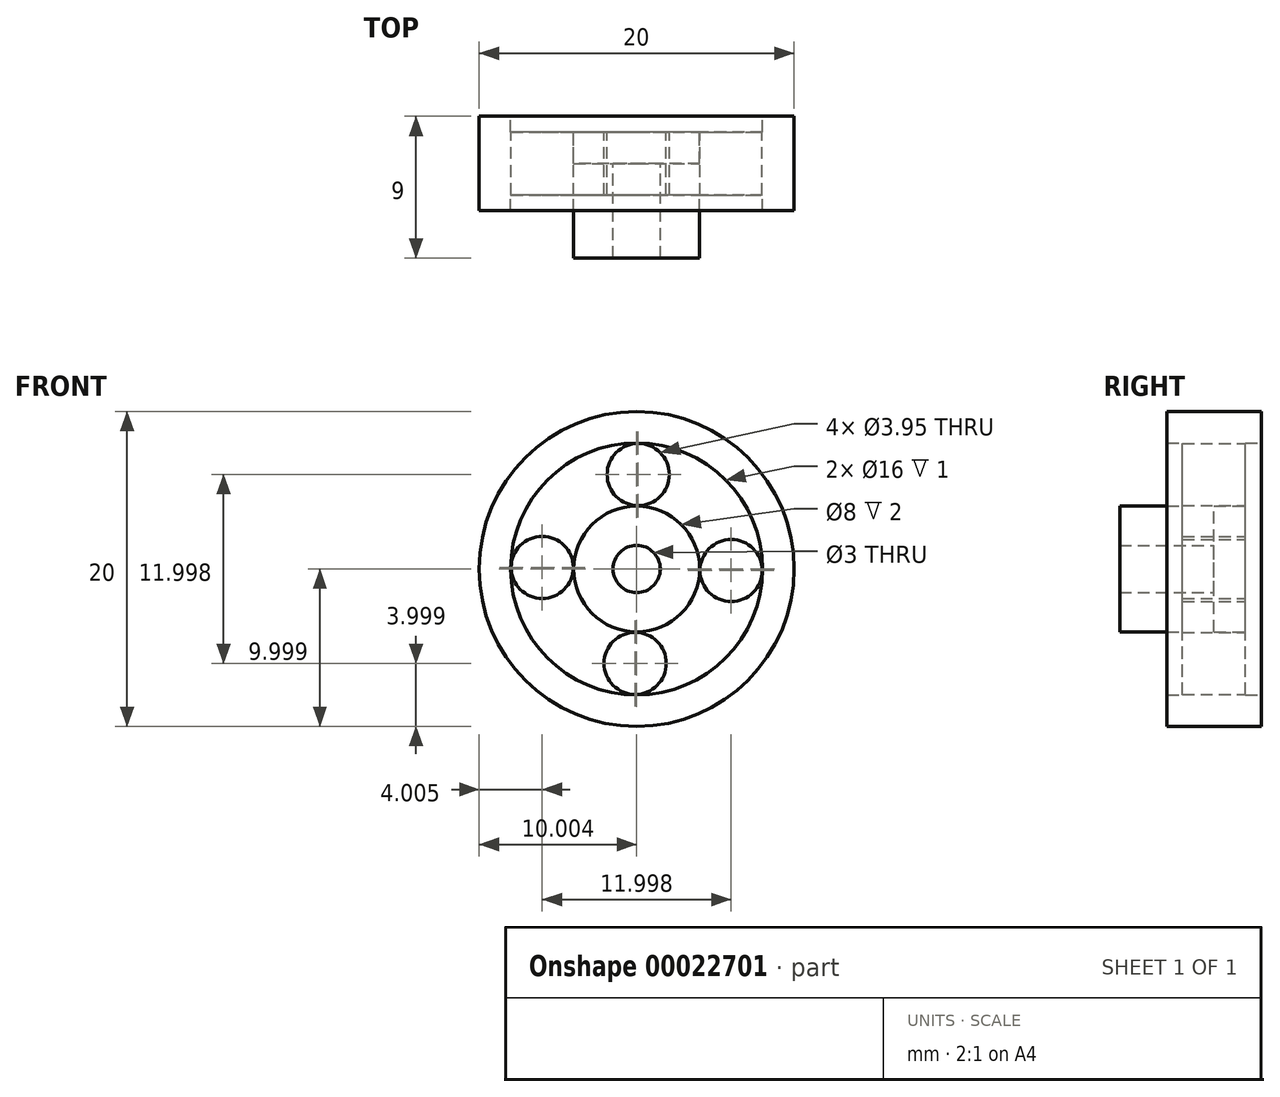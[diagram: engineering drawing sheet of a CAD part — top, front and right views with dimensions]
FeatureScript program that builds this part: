
annotation { "Feature Type Name" : "Feature", "Feature Type Description" : "" }
export const myFeature = defineFeature(function(context is Context, id is Id, definition is map)
    precondition{}
    {
        {
            var Q0;
            Q0=qCreatedBy(makeId("Front.planeOp"),FACE);
            var sketch = newSketch(context, id + "F0", { "sketchPlane" : qUnion([Q0])});
            skPoint(sketch, "E0.center", {"position": v(88.66, 19.89) * mm});
            skCircle(sketch, "E1", {"center": v(88.66, 19.89) * mm, "radius": 10 * mm});
            skCircle(sketch, "E2", {"center": v(88.66, 19.89) * mm, "radius": 1.5 * mm});
            skCircle(sketch, "E3", {"center": v(88.66, 19.89) * mm, "radius": 8 * mm});
            skCircle(sketch, "E4", {"center": v(88.66, 19.89) * mm, "radius": 4 * mm});
            skLineSegment(sketch, "E5", {"start": v(88.76, 23.89) * mm, "end": v(88.76, 23.91) * mm});
            skCircle(sketch, "E6", {"center": v(88.76, 25.89) * mm, "radius": 1.97 * mm});
            skLineSegment(sketch, "E7.trimOffspring", {"start": v(88.76, 27.86) * mm, "end": v(88.76, 27.89) * mm});
            skCircle(sketch, "E8.1.0", {"center": v(82.66, 19.99) * mm, "radius": 1.97 * mm});
            skCircle(sketch, "E8.2.0", {"center": v(88.57, 13.89) * mm, "radius": 1.97 * mm});
            skCircle(sketch, "E8.3.0", {"center": v(94.66, 19.8) * mm, "radius": 1.97 * mm});
            skSolve(sketch);
        }
        {
            var Q0;
            Q0=makeQuery(id+"F0.imprint","IMPRINT",FACE,{"disambiguationData":[TD([[makeQuery(id+"F0.imprint","IMPRINT",EDGE,{"derivedFrom":sQuery(id+"F0.wireOp",EDGE,"E1")}),1.0]])]});
            extrude(context, id + "F1", {"entities" : qUnion([Q0]), "endBound" : BoundingType.SYMMETRIC, "depth" : 6 * mm});
        }
        {
            var Q0;
            Q0=makeQuery(id+"F0.imprint","IMPRINT",FACE,{"disambiguationData":[TD([[makeQuery(id+"F0.imprint","IMPRINT",EDGE,{"derivedFrom":sQuery(id+"F0.wireOp",EDGE,"E3")}),1.0]])]});
            extrude(context, id + "F2", {"entities" : qUnion([Q0]), "operationType" : NewBodyOperationType.ADD, "endBound" : BoundingType.SYMMETRIC, "depth" : 4 * mm});
        }
        {
            var Q0;
            Q0=makeQuery(id+"F0.imprint","IMPRINT",FACE,{"disambiguationData":[TD([[makeQuery(id+"F0.imprint","IMPRINT",EDGE,{"derivedFrom":sQuery(id+"F0.wireOp",EDGE,"E2")}),-1.0]])]});
            extrude(context, id + "F3", {"entities" : qUnion([Q0]), "operationType" : NewBodyOperationType.ADD, "depth" : 6 * mm});
        }
    });
